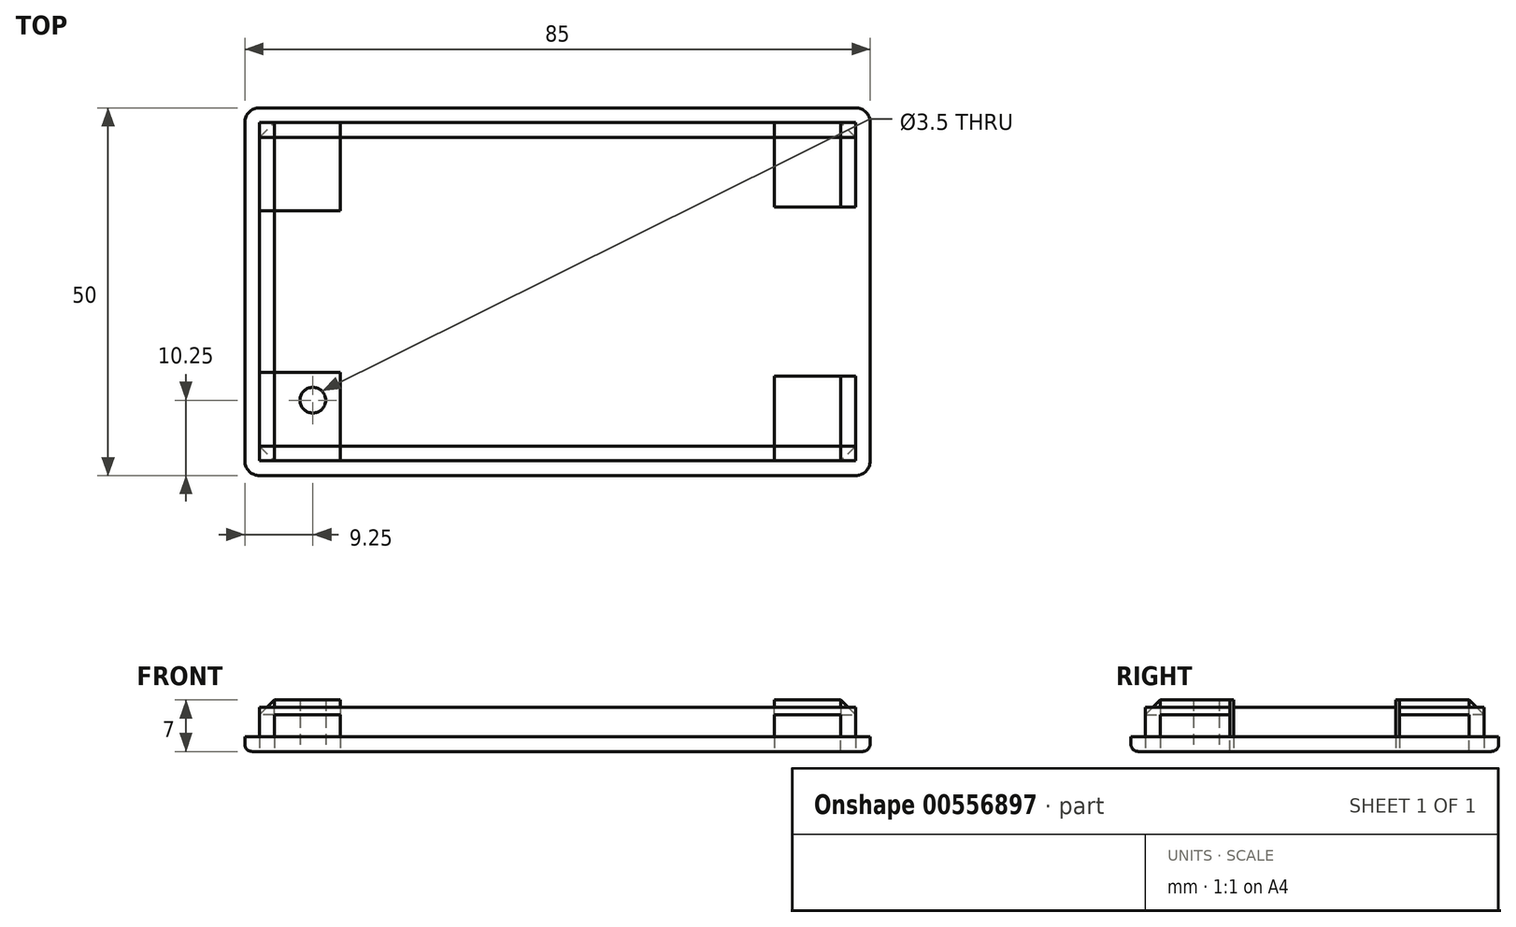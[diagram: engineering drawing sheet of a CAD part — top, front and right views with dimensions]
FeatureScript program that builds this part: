
annotation { "Feature Type Name" : "Feature", "Feature Type Description" : "" }
export const myFeature = defineFeature(function(context is Context, id is Id, definition is map)
    precondition{}
    {
        {
            var Q0;
            Q0=qCreatedBy(makeId("Top.planeOp"),FACE);
            var sketch = newSketch(context, id + "F0", { "sketchPlane" : qUnion([Q0])});
            skLineSegment(sketch, "E0.bottom", {"start": v(-42.5, 25) * mm, "end": v(42.5, 25) * mm});
            skLineSegment(sketch, "E0.top", {"start": v(-42.5, -25) * mm, "end": v(42.5, -25) * mm});
            skLineSegment(sketch, "E0.left", {"start": v(-42.5, 25) * mm, "end": v(-42.5, -25) * mm});
            skLineSegment(sketch, "E0.right", {"start": v(42.5, 25) * mm, "end": v(42.5, -25) * mm});
            skSolve(sketch);
        }
        {
            var Q0;
            Q0=qCreatedBy(makeId("Top.planeOp"),FACE);
            var sketch = newSketch(context, id + "F1", { "sketchPlane" : qUnion([Q0])});
            skCircle(sketch, "E1", {"center": v(34, 7.5) * mm, "radius": 3.04 * mm});
            skCircle(sketch, "E2", {"center": v(34, -7.5) * mm, "radius": 3.04 * mm});
            skCircle(sketch, "E3", {"center": v(34, 0) * mm, "radius": 3.04 * mm});
            skSolve(sketch);
        }
        {
            var Q0;
            Q0=qCreatedBy(makeId("Top.planeOp"),FACE);
            var sketch = newSketch(context, id + "F2", { "sketchPlane" : qUnion([Q0])});
            skCircle(sketch, "E4", {"center": v(-23, 0) * mm, "radius": 2.5 * mm});
            skCircle(sketch, "E5", {"center": v(15, 0) * mm, "radius": 2.5 * mm});
            skSolve(sketch);
        }
        {
            var Q0;
            Q0=qCreatedBy(makeId("Top.planeOp"),FACE);
            var sketch = newSketch(context, id + "F3", { "sketchPlane" : qUnion([Q0])});
            skCircle(sketch, "E6", {"center": v(-33.25, 14.75) * mm, "radius": 1.75 * mm});
            skCircle(sketch, "E7", {"center": v(-33.25, -14.75) * mm, "radius": 1.75 * mm});
            skCircle(sketch, "E8", {"center": v(33.25, 14.75) * mm, "radius": 1.75 * mm});
            skCircle(sketch, "E9", {"center": v(33.25, -14.75) * mm, "radius": 1.75 * mm});
            skSolve(sketch);
        }
        {
            var Q0;
            Q0=qCreatedBy(makeId("Top.planeOp"),FACE);
            var sketch = newSketch(context, id + "F4", { "sketchPlane" : qUnion([Q0])});
            skLineSegment(sketch, "E10.bottom", {"start": v(-40.5, 23) * mm, "end": v(40.5, 23) * mm});
            skLineSegment(sketch, "E10.top", {"start": v(-40.5, -23) * mm, "end": v(40.5, -23) * mm});
            skLineSegment(sketch, "E10.left", {"start": v(-40.5, 23) * mm, "end": v(-40.5, -23) * mm});
            skLineSegment(sketch, "E10.right", {"start": v(40.5, 23) * mm, "end": v(40.5, -23) * mm});
            skSolve(sketch);
        }
        {
            var Q0;
            Q0=qCreatedBy(makeId("Top.planeOp"),FACE);
            var sketch = newSketch(context, id + "F5", { "sketchPlane" : qUnion([Q0])});
            skLineSegment(sketch, "E11.bottom", {"start": v(-38.5, 21) * mm, "end": v(38.5, 21) * mm});
            skLineSegment(sketch, "E11.top", {"start": v(-38.5, -21) * mm, "end": v(38.5, -21) * mm});
            skLineSegment(sketch, "E11.left", {"start": v(-38.5, 21) * mm, "end": v(-38.5, -21) * mm});
            skLineSegment(sketch, "E11.right", {"start": v(38.5, 21) * mm, "end": v(38.5, -21) * mm});
            skSolve(sketch);
        }
        {
            var Q0;
            Q0=qCreatedBy(makeId("Top.planeOp"),FACE);
            var sketch = newSketch(context, id + "F6", { "sketchPlane" : qUnion([Q0])});
            skLineSegment(sketch, "E12.bottom", {"start": v(31.7, 11.5) * mm, "end": v(46.45, 11.5) * mm});
            skLineSegment(sketch, "E12.top", {"start": v(31.7, -11.5) * mm, "end": v(46.45, -11.5) * mm});
            skLineSegment(sketch, "E12.left", {"start": v(31.7, 11.5) * mm, "end": v(31.7, -11.5) * mm});
            skLineSegment(sketch, "E12.right", {"start": v(46.45, 11.5) * mm, "end": v(46.45, -11.5) * mm});
            skSolve(sketch);
        }
        {
            var Q0;
            Q0=qCreatedBy(makeId("Top.planeOp"),FACE);
            var sketch = newSketch(context, id + "F7", { "sketchPlane" : qUnion([Q0])});
            skLineSegment(sketch, "E13.bottom", {"start": v(-40.5, -11) * mm, "end": v(-29.5, -11) * mm});
            skLineSegment(sketch, "E13.top", {"start": v(-40.5, -23) * mm, "end": v(-29.5, -23) * mm});
            skLineSegment(sketch, "E13.left", {"start": v(-40.5, -11) * mm, "end": v(-40.5, -23) * mm});
            skLineSegment(sketch, "E13.right", {"start": v(-29.5, -11) * mm, "end": v(-29.5, -23) * mm});
            skLineSegment(sketch, "E14.bottom", {"start": v(29.5, -11.5) * mm, "end": v(40.5, -11.5) * mm});
            skLineSegment(sketch, "E14.top", {"start": v(29.5, -23) * mm, "end": v(40.5, -23) * mm});
            skLineSegment(sketch, "E14.left", {"start": v(29.5, -11.5) * mm, "end": v(29.5, -23) * mm});
            skLineSegment(sketch, "E14.right", {"start": v(40.5, -11.5) * mm, "end": v(40.5, -23) * mm});
            skLineSegment(sketch, "E15.bottom", {"start": v(29.5, 23) * mm, "end": v(40.5, 23) * mm});
            skLineSegment(sketch, "E15.top", {"start": v(29.5, 11.5) * mm, "end": v(40.5, 11.5) * mm});
            skLineSegment(sketch, "E15.left", {"start": v(29.5, 23) * mm, "end": v(29.5, 11.5) * mm});
            skLineSegment(sketch, "E15.right", {"start": v(40.5, 23) * mm, "end": v(40.5, 11.5) * mm});
            skLineSegment(sketch, "E16.bottom", {"start": v(-40.5, 23) * mm, "end": v(-29.5, 23) * mm});
            skLineSegment(sketch, "E16.top", {"start": v(-40.5, 11) * mm, "end": v(-29.5, 11) * mm});
            skLineSegment(sketch, "E16.left", {"start": v(-40.5, 23) * mm, "end": v(-40.5, 11) * mm});
            skLineSegment(sketch, "E16.right", {"start": v(-29.5, 23) * mm, "end": v(-29.5, 11) * mm});
            skSolve(sketch);
        }
        {
            var Q0;
            Q0=qSketchRegion(id+"F0",true);
            extrude(context, id + "F8", {"entities" : qUnion([Q0]), "depth" : 2 * mm, "offsetDistance" : 25 * mm});
        }
        {
            var Q0;
            Q0=makeQuery(id+"F8.opExtrude","CAP_EDGE",EDGE,{"disambiguationData":[OSD([sQuery(id+"F0.wireOp",EDGE,"E0.top")])],"isStart":true});
            var Q1;
            Q1=makeQuery(id+"F8.opExtrude","CAP_EDGE",EDGE,{"disambiguationData":[OSD([sQuery(id+"F0.wireOp",EDGE,"E0.right")])],"isStart":true});
            var Q2;
            Q2=makeQuery(id+"F8.opExtrude","CAP_EDGE",EDGE,{"disambiguationData":[OSD([sQuery(id+"F0.wireOp",EDGE,"E0.bottom")])],"isStart":true});
            var Q3;
            Q3=makeQuery(id+"F8.opExtrude","CAP_EDGE",EDGE,{"disambiguationData":[OSD([sQuery(id+"F0.wireOp",EDGE,"E0.left")])],"isStart":true});
            fillet(context, id + "F9", {"entities" : qUnion([Q0, Q1, Q2, Q3]), "radius" : 1 * mm, "tangentPropagation" : true, "allowEdgeOverflow" : false});
        }
        {
            var Q0;
            Q0=makeQuery(id+"F8.opExtrude","SWEPT_EDGE",EDGE,{"disambiguationData":[OSD([sQuery(id+"F0.wireOp",EDGE,"E0.bottom"),sQuery(id+"F0.wireOp",EDGE,"E0.right")])]});
            var Q1;
            Q1=makeQuery(id+"F8.opExtrude","SWEPT_EDGE",EDGE,{"disambiguationData":[OSD([sQuery(id+"F0.wireOp",EDGE,"E0.bottom"),sQuery(id+"F0.wireOp",EDGE,"E0.left")])]});
            var Q2;
            Q2=makeQuery(id+"F8.opExtrude","SWEPT_EDGE",EDGE,{"disambiguationData":[OSD([sQuery(id+"F0.wireOp",EDGE,"E0.top"),sQuery(id+"F0.wireOp",EDGE,"E0.left")])]});
            var Q3;
            Q3=makeQuery(id+"F8.opExtrude","SWEPT_EDGE",EDGE,{"disambiguationData":[OSD([sQuery(id+"F0.wireOp",EDGE,"E0.top"),sQuery(id+"F0.wireOp",EDGE,"E0.right")])]});
            fillet(context, id + "F10", {"entities" : qUnion([Q0, Q1, Q2, Q3]), "radius" : 2 * mm, "tangentPropagation" : true, "allowEdgeOverflow" : false});
        }
        {
            var Q0;
            Q0=qSketchRegion(id+"F1",true);
            extrude(context, id + "F11", {"entities" : qUnion([Q0]), "depth" : 5 * mm, "offsetDistance" : 25 * mm});
        }
        {
            var Q0;
            Q0=qSketchRegion(id+"F2",true);
            extrude(context, id + "F12", {"entities" : qUnion([Q0]), "depth" : 5 * mm, "offsetDistance" : 25 * mm});
        }
        {
            var Q0;
            Q0=qSketchRegion(id+"F4",true);
            extrude(context, id + "F13", {"entities" : qUnion([Q0]), "depth" : 6 * mm, "offsetDistance" : 25 * mm});
        }
        {
            var Q0;
            Q0=qSketchRegion(id+"F5",true);
            extrude(context, id + "F14", {"entities" : qUnion([Q0]), "depth" : 6 * mm, "offsetDistance" : 25 * mm});
        }
        {
            var Q0;
            Q0=qSketchRegion(id+"F6",true);
            extrude(context, id + "F15", {"entities" : qUnion([Q0]), "depth" : 6 * mm, "offsetDistance" : 25 * mm});
        }
        {
            var Q0;
            Q0=makeQuery(id+"F7.imprint","IMPRINT",FACE,{"disambiguationData":[TD([[makeQuery(id+"F7.imprint","IMPRINT",EDGE,{"derivedFrom":sQuery(id+"F7.wireOp",EDGE,"E13.bottom")}),-1.0]])]});
            var Q1;
            Q1=makeQuery(id+"F7.imprint","IMPRINT",FACE,{"disambiguationData":[TD([[makeQuery(id+"F7.imprint","IMPRINT",EDGE,{"derivedFrom":sQuery(id+"F7.wireOp",EDGE,"E16.bottom")}),-1.0]])]});
            var Q2;
            Q2=makeQuery(id+"F7.imprint","IMPRINT",FACE,{"disambiguationData":[TD([[makeQuery(id+"F7.imprint","IMPRINT",EDGE,{"derivedFrom":sQuery(id+"F7.wireOp",EDGE,"E15.bottom")}),-1.0]])]});
            var Q3;
            Q3=makeQuery(id+"F7.imprint","IMPRINT",FACE,{"disambiguationData":[TD([[makeQuery(id+"F7.imprint","IMPRINT",EDGE,{"derivedFrom":sQuery(id+"F7.wireOp",EDGE,"E14.bottom")}),-1.0]])]});
            extrude(context, id + "F16", {"entities" : qUnion([Q0, Q1, Q2, Q3]), "depth" : 7 * mm, "offsetDistance" : 25 * mm});
        }
        {
            var Q0;
            Q0=makeQuery(id+"F3.imprint","IMPRINT",FACE,{"disambiguationData":[TD([[makeQuery(id+"F3.imprint","IMPRINT",EDGE,{"derivedFrom":sQuery(id+"F3.wireOp",EDGE,"E7")}),1.0]])]});
            var Q1;
            Q1=makeQuery(id+"F3.imprint","IMPRINT",FACE,{"disambiguationData":[TD([[makeQuery(id+"F3.imprint","IMPRINT",EDGE,{"derivedFrom":sQuery(id+"F3.wireOp",EDGE,"E9")}),1.0]])]});
            var Q2;
            Q2=makeQuery(id+"F3.imprint","IMPRINT",FACE,{"disambiguationData":[TD([[makeQuery(id+"F3.imprint","IMPRINT",EDGE,{"derivedFrom":sQuery(id+"F3.wireOp",EDGE,"E8")}),1.0]])]});
            var Q3;
            Q3=makeQuery(id+"F3.imprint","IMPRINT",FACE,{"disambiguationData":[TD([[makeQuery(id+"F3.imprint","IMPRINT",EDGE,{"derivedFrom":sQuery(id+"F3.wireOp",EDGE,"E6")}),1.0]])]});
            extrude(context, id + "F17", {"entities" : qUnion([Q0, Q1, Q2, Q3]), "depth" : 8 * mm, "offsetDistance" : 25 * mm});
        }
        {
            var Q0;
            Q0=makeQuery(id+"F14.opExtrude","SWEPT_BODY",BODY,{"disambiguationData":[OSD([sQuery(id+"F5.wireOp",EDGE,"E11.bottom"),sQuery(id+"F5.wireOp",EDGE,"E11.top"),sQuery(id+"F5.wireOp",EDGE,"E11.left"),sQuery(id+"F5.wireOp",EDGE,"E11.right")])]});
            var Q1;
            Q1=makeQuery(id+"F13.opExtrude","SWEPT_BODY",BODY,{"disambiguationData":[OSD([sQuery(id+"F4.wireOp",EDGE,"E10.bottom"),sQuery(id+"F4.wireOp",EDGE,"E10.top"),sQuery(id+"F4.wireOp",EDGE,"E10.left"),sQuery(id+"F4.wireOp",EDGE,"E10.right")])]});
            booleanBodies(context, id + "F18", {"operationType" : BooleanOperationType.SUBTRACTION, "tools" : qUnion([Q0]), "targets" : qUnion([Q1])});
        }
        {
            var Q0;
            Q0=makeQuery(id+"F15.opExtrude","SWEPT_BODY",BODY,{"disambiguationData":[OSD([sQuery(id+"F6.wireOp",EDGE,"E12.bottom"),sQuery(id+"F6.wireOp",EDGE,"E12.top"),sQuery(id+"F6.wireOp",EDGE,"E12.left"),sQuery(id+"F6.wireOp",EDGE,"E12.right")])]});
            var Q1;
            Q1=makeQuery(id+"F13.opExtrude","SWEPT_BODY",BODY,{"disambiguationData":[OSD([sQuery(id+"F4.wireOp",EDGE,"E10.bottom"),sQuery(id+"F4.wireOp",EDGE,"E10.top"),sQuery(id+"F4.wireOp",EDGE,"E10.left"),sQuery(id+"F4.wireOp",EDGE,"E10.right")])]});
            booleanBodies(context, id + "F19", {"operationType" : BooleanOperationType.SUBTRACTION, "tools" : qUnion([Q0]), "targets" : qUnion([Q1])});
        }
        {
            var Q0;
            Q0=makeQuery(id+"F11.opExtrude","SWEPT_BODY",BODY,{"disambiguationData":[OSD([sQuery(id+"F1.wireOp",EDGE,"E1")])]});
            var Q1;
            Q1=makeQuery(id+"F11.opExtrude","SWEPT_BODY",BODY,{"disambiguationData":[OSD([sQuery(id+"F1.wireOp",EDGE,"E3")])]});
            var Q2;
            Q2=makeQuery(id+"F11.opExtrude","SWEPT_BODY",BODY,{"disambiguationData":[OSD([sQuery(id+"F1.wireOp",EDGE,"E2")])]});
            var Q3;
            Q3=makeQuery(id+"F16.opExtrude","SWEPT_BODY",BODY,{"disambiguationData":[OSD([sQuery(id+"F7.wireOp",EDGE,"E13.bottom"),sQuery(id+"F7.wireOp",EDGE,"E13.top"),sQuery(id+"F7.wireOp",EDGE,"E13.left"),sQuery(id+"F7.wireOp",EDGE,"E13.right")])]});
            booleanBodies(context, id + "F20", {"operationType" : BooleanOperationType.SUBTRACTION, "tools" : qUnion([Q0, Q1, Q2]), "targets" : qUnion([Q3])});
        }
        {
            var Q0;
            Q0=makeQuery(id+"F12.opExtrude","SWEPT_BODY",BODY,{"disambiguationData":[OSD([sQuery(id+"F2.wireOp",EDGE,"E4")])]});
            var Q1;
            Q1=makeQuery(id+"F12.opExtrude","SWEPT_BODY",BODY,{"disambiguationData":[OSD([sQuery(id+"F2.wireOp",EDGE,"E5")])]});
            var Q2;
            Q2=makeQuery(id+"F16.opExtrude","SWEPT_BODY",BODY,{"disambiguationData":[OSD([sQuery(id+"F7.wireOp",EDGE,"E13.bottom"),sQuery(id+"F7.wireOp",EDGE,"E13.top"),sQuery(id+"F7.wireOp",EDGE,"E13.left"),sQuery(id+"F7.wireOp",EDGE,"E13.right")])]});
            booleanBodies(context, id + "F21", {"operationType" : BooleanOperationType.SUBTRACTION, "tools" : qUnion([Q0, Q1]), "targets" : qUnion([Q2])});
        }
        {
            var Q0;
            Q0=makeQuery(id+"F17.opExtrude","SWEPT_BODY",BODY,{"disambiguationData":[OSD([sQuery(id+"F3.wireOp",EDGE,"E7")])]});
            var Q1;
            Q1=makeQuery(id+"F17.opExtrude","SWEPT_BODY",BODY,{"disambiguationData":[OSD([sQuery(id+"F3.wireOp",EDGE,"E6")])]});
            var Q2;
            Q2=makeQuery(id+"F17.opExtrude","SWEPT_BODY",BODY,{"disambiguationData":[OSD([sQuery(id+"F3.wireOp",EDGE,"E8")])]});
            var Q3;
            Q3=makeQuery(id+"F17.opExtrude","SWEPT_BODY",BODY,{"disambiguationData":[OSD([sQuery(id+"F3.wireOp",EDGE,"E9")])]});
            var Q4;
            Q4=makeQuery(id+"F16.opExtrude","SWEPT_BODY",BODY,{"disambiguationData":[OSD([sQuery(id+"F7.wireOp",EDGE,"E13.bottom"),sQuery(id+"F7.wireOp",EDGE,"E13.top"),sQuery(id+"F7.wireOp",EDGE,"E13.left"),sQuery(id+"F7.wireOp",EDGE,"E13.right")])]});
            booleanBodies(context, id + "F22", {"operationType" : BooleanOperationType.SUBTRACTION, "tools" : qUnion([Q0, Q1, Q2, Q3]), "targets" : qUnion([Q4])});
        }
        {
            var Q0;
            Q0=makeQuery(id+"F16.opExtrude","SWEPT_EDGE",EDGE,{"disambiguationData":[OSD([sQuery(id+"F7.wireOp",EDGE,"E14.top"),sQuery(id+"F7.wireOp",EDGE,"E14.right")])]});
            var Q1;
            Q1=makeQuery(id+"F16.opExtrude","CAP_EDGE",EDGE,{"disambiguationData":[OSD([sQuery(id+"F7.wireOp",EDGE,"E14.top")])],"isStart":false});
            var Q2;
            Q2=makeQuery(id+"F16.opExtrude","CAP_EDGE",EDGE,{"disambiguationData":[OSD([sQuery(id+"F7.wireOp",EDGE,"E14.right")])],"isStart":false});
            var Q3;
            Q3=makeQuery(id+"F16.opExtrude","CAP_EDGE",EDGE,{"disambiguationData":[OSD([sQuery(id+"F7.wireOp",EDGE,"E13.top")])],"isStart":false});
            var Q4;
            Q4=makeQuery(id+"F16.opExtrude","SWEPT_EDGE",EDGE,{"disambiguationData":[OSD([sQuery(id+"F7.wireOp",EDGE,"E13.top"),sQuery(id+"F7.wireOp",EDGE,"E13.left")])]});
            var Q5;
            Q5=makeQuery(id+"F16.opExtrude","CAP_EDGE",EDGE,{"disambiguationData":[OSD([sQuery(id+"F7.wireOp",EDGE,"E13.left")])],"isStart":false});
            var Q6;
            Q6=makeQuery(id+"F16.opExtrude","CAP_EDGE",EDGE,{"disambiguationData":[OSD([sQuery(id+"F7.wireOp",EDGE,"E16.left")])],"isStart":false});
            var Q7;
            Q7=makeQuery(id+"F16.opExtrude","CAP_EDGE",EDGE,{"disambiguationData":[OSD([sQuery(id+"F7.wireOp",EDGE,"E16.bottom")])],"isStart":false});
            var Q8;
            Q8=makeQuery(id+"F16.opExtrude","SWEPT_EDGE",EDGE,{"disambiguationData":[OSD([sQuery(id+"F7.wireOp",EDGE,"E16.bottom"),sQuery(id+"F7.wireOp",EDGE,"E16.left")])]});
            var Q9;
            Q9=makeQuery(id+"F16.opExtrude","CAP_EDGE",EDGE,{"disambiguationData":[OSD([sQuery(id+"F7.wireOp",EDGE,"E15.bottom")])],"isStart":false});
            var Q10;
            Q10=makeQuery(id+"F16.opExtrude","SWEPT_EDGE",EDGE,{"disambiguationData":[OSD([sQuery(id+"F7.wireOp",EDGE,"E15.bottom"),sQuery(id+"F7.wireOp",EDGE,"E15.right")])]});
            var Q11;
            Q11=makeQuery(id+"F16.opExtrude","CAP_EDGE",EDGE,{"disambiguationData":[OSD([sQuery(id+"F7.wireOp",EDGE,"E15.right")])],"isStart":false});
            chamfer(context, id + "F23", {"entities" : qUnion([Q0, Q1, Q2, Q3, Q4, Q5, Q6, Q7, Q8, Q9, Q10, Q11]), "width" : 2 * mm, "tangentPropagation" : true});
        }
    });
